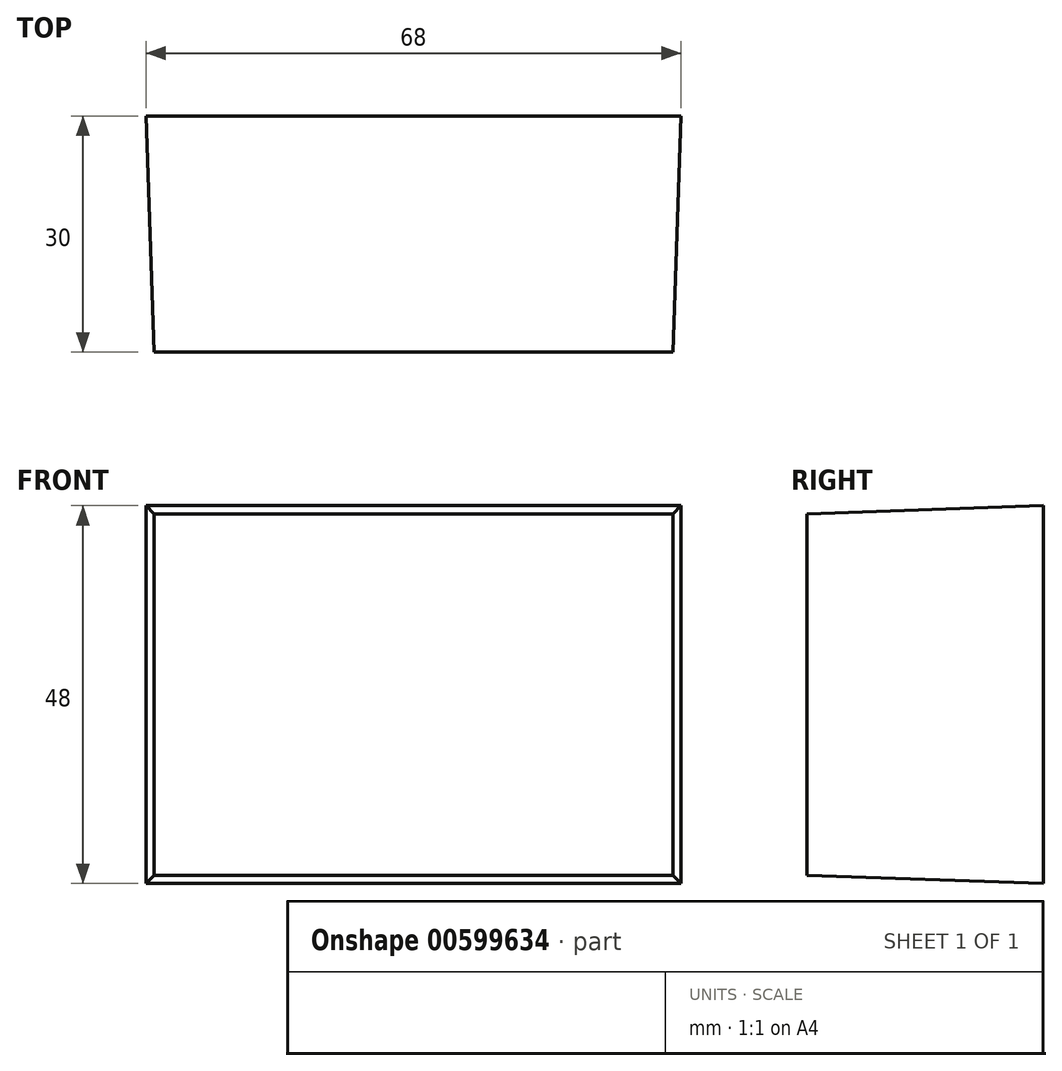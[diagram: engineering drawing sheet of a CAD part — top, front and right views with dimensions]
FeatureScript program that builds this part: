
annotation { "Feature Type Name" : "Feature", "Feature Type Description" : "" }
export const myFeature = defineFeature(function(context is Context, id is Id, definition is map)
    precondition{}
    {
        {
            var Q0;
            Q0=qCreatedBy(makeId("Front.planeOp"),FACE);
            var sketch = newSketch(context, id + "F0", { "sketchPlane" : qUnion([Q0])});
            skLineSegment(sketch, "E0.bottom", {"start": v(-34, 24) * mm, "end": v(34, 24) * mm});
            skLineSegment(sketch, "E0.top", {"start": v(-34, -24) * mm, "end": v(34, -24) * mm});
            skLineSegment(sketch, "E0.left", {"start": v(-34, 24) * mm, "end": v(-34, -24) * mm});
            skLineSegment(sketch, "E0.right", {"start": v(34, 24) * mm, "end": v(34, -24) * mm});
            skPoint(sketch, "E0.middle", {"position": v(0, 0) * mm});
            skLineSegment(sketch, "E1", {"start": v(-34, 20.32) * mm, "end": v(34, 20.32) * mm, "construction": true});
            skSolve(sketch);
        }
        {
            var Q0;
            Q0=makeQuery(id+"F0.imprint","IMPRINT",FACE,{"disambiguationData":[TD([[makeQuery(id+"F0.imprint","IMPRINT",EDGE,{"derivedFrom":sQuery(id+"F0.wireOp",EDGE,"E0.bottom")}),-1.0]])]});
            extrude(context, id + "F1", {"entities" : qUnion([Q0]), "depth" : 30 * mm, "offsetDistance" : 25.4 * mm, "hasDraft" : true, "draftAngle" : 2 * degree, "draftPullDirection" : true});
        }
    });
